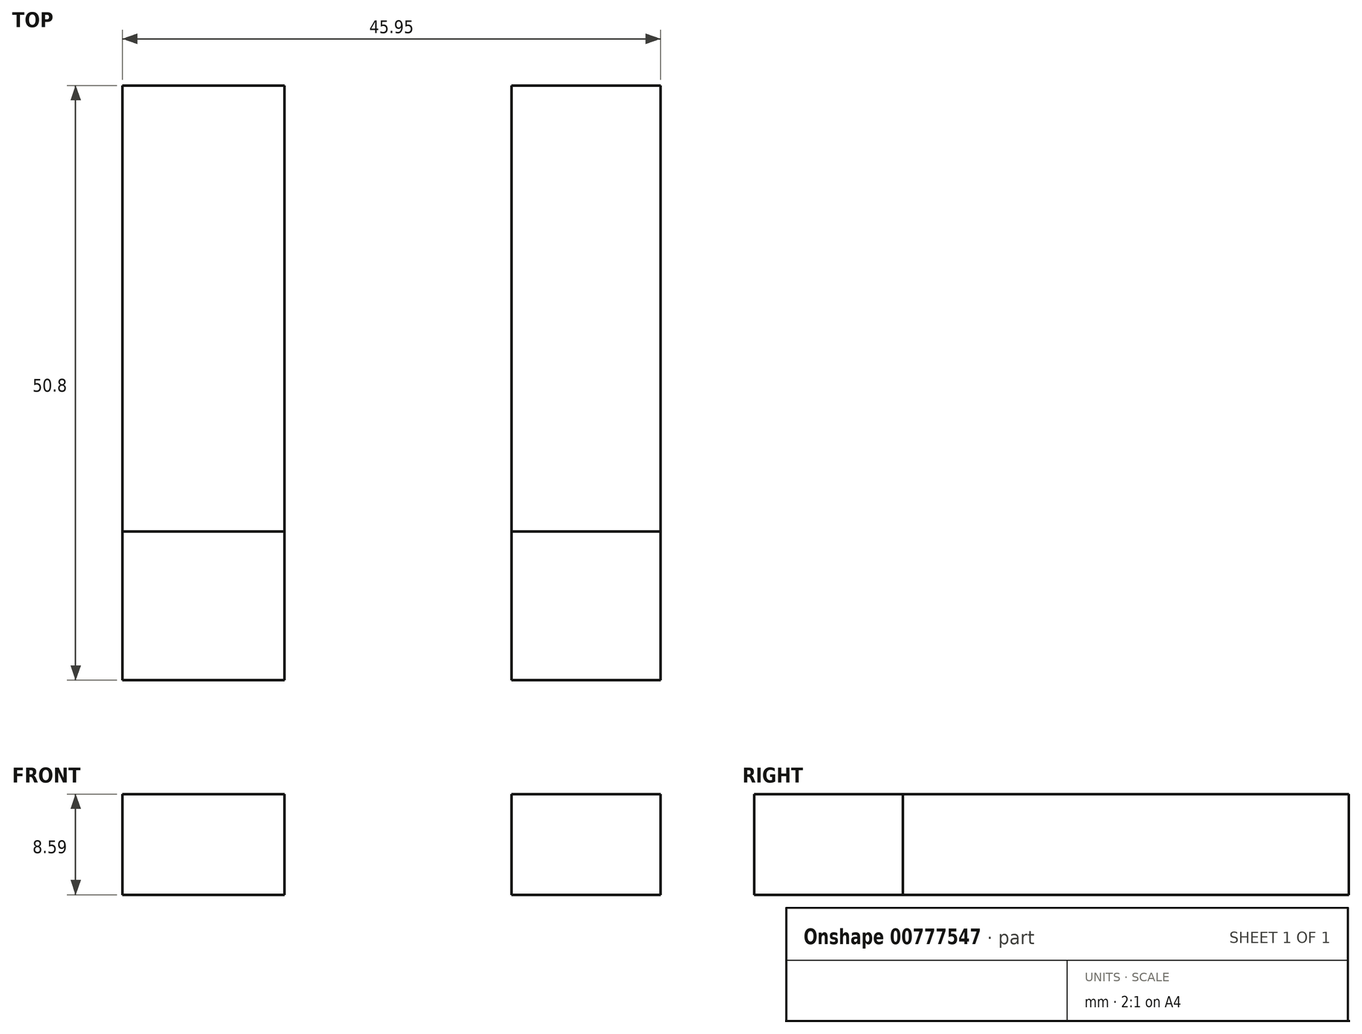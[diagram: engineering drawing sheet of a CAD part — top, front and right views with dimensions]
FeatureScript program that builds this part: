
annotation { "Feature Type Name" : "Feature", "Feature Type Description" : "" }
export const myFeature = defineFeature(function(context is Context, id is Id, definition is map)
    precondition{}
    {
        {
            var Q0;
            Q0=qCreatedBy(makeId("Front.planeOp"),FACE);
            var sketch = newSketch(context, id + "F0", { "sketchPlane" : qUnion([Q0])});
            skLineSegment(sketch, "E0.bottom", {"start": v(-58.62, -49.49) * mm, "end": v(-44.78, -49.49) * mm});
            skLineSegment(sketch, "E0.top", {"start": v(-58.62, -40.9) * mm, "end": v(-44.78, -40.9) * mm});
            skLineSegment(sketch, "E0.left", {"start": v(-58.62, -49.49) * mm, "end": v(-58.62, -40.9) * mm});
            skLineSegment(sketch, "E0.right", {"start": v(-44.78, -49.49) * mm, "end": v(-44.78, -40.9) * mm});
            skLineSegment(sketch, "E1.bottom", {"start": v(-25.4, -40.9) * mm, "end": v(-12.67, -40.9) * mm});
            skLineSegment(sketch, "E1.top", {"start": v(-25.4, -49.49) * mm, "end": v(-12.67, -49.49) * mm});
            skLineSegment(sketch, "E1.left", {"start": v(-25.4, -40.9) * mm, "end": v(-25.4, -49.49) * mm});
            skLineSegment(sketch, "E1.right", {"start": v(-12.67, -40.9) * mm, "end": v(-12.67, -49.49) * mm});
            skSolve(sketch);
        }
        {
            var Q0;
            Q0 = qSketchRegion(id + "F0", true);
            extrude(context, id + "F1", {"entities" : qUnion([Q0]), "depth" : 50.8 * mm, "offsetDistance" : 25.4 * mm});
        }
        {
            var Q0;
            Q0 = qSketchRegion(id + "F0", true);
            extrude(context, id + "F2", {"entities" : qUnion([Q0]), "depth" : 38.1 * mm, "offsetDistance" : 25.4 * mm});
        }
    });
